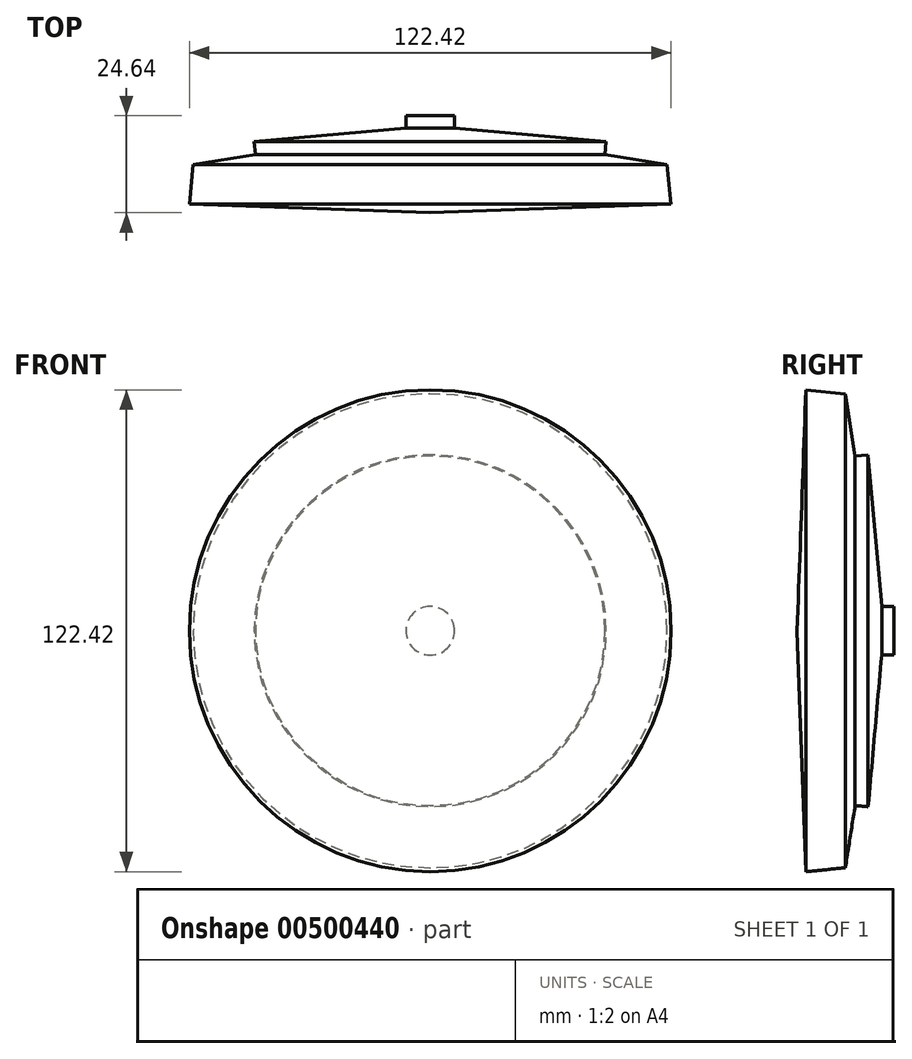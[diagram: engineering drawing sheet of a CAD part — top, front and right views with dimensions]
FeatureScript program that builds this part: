
annotation { "Feature Type Name" : "Feature", "Feature Type Description" : "" }
export const myFeature = defineFeature(function(context is Context, id is Id, definition is map)
    precondition{}
    {
        {
            var Q0;
            Q0=qCreatedBy(makeId("Top.planeOp"),FACE);
            var sketch = newSketch(context, id + "F0", { "sketchPlane" : qUnion([Q0])});
            skLineSegment(sketch, "E0", {"start": v(0, 0) * mm, "end": v(0, 39.52) * mm});
            skLineSegment(sketch, "E1", {"start": v(0, 39.52) * mm, "end": v(-6.2, 39.52) * mm});
            skLineSegment(sketch, "E2", {"start": v(-6.2, 39.52) * mm, "end": v(-6.2, 36.36) * mm});
            skLineSegment(sketch, "E3", {"start": v(-6.2, 36.36) * mm, "end": v(-44.7, 32.92) * mm});
            skLineSegment(sketch, "E4", {"start": v(-44.7, 32.92) * mm, "end": v(-44.4, 29.6) * mm});
            skLineSegment(sketch, "E5", {"start": v(-44.4, 29.6) * mm, "end": v(-60.2, 27.14) * mm});
            skLineSegment(sketch, "E6", {"start": v(-60.2, 27.14) * mm, "end": v(-61.21, 17.1) * mm});
            skLineSegment(sketch, "E7", {"start": v(-61.21, 17.1) * mm, "end": v(0, 14.88) * mm});
            skSolve(sketch);
        }
        {
            var Q0;
            Q0 = qSketchRegion(id + "F0", true);
            var Q1;
            Q1=sQuery(id+"F0.wireOp",EDGE,"E0");
            revolve(context, id + "F1", {"entities" : qUnion([Q0]), "axis" : qUnion([Q1]), "revolveType" : RevolveType.FULL});
        }
    });
